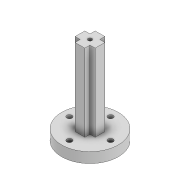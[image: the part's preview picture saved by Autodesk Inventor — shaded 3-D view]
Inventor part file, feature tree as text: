
AUTODESK INVENTOR PART (.ipt)
format: ipt  version: 2022 (Build 260153000, 153)  size: 144,896 bytes
history: native  units: mm
features: extrude x6, sketch x6, pattern_circular x1
ambient origin geometry x8: Origin, YZ Plane, XZ Plane, XY Plane, X Axis, Y Axis, Z Axis, Center Point
bodies: Solid1 (feature_tree)
feature tree (13):
  extrude  "Extrusion1"  Depth=4.0mm TaperAngle=0.0deg
  extrude  "Extrusion2"  Depth=8.0mm
  pattern_circular  "Circular Pattern1"  Count=4 Angle=360.0deg
  extrude  "Extrusion3"  Depth=7.8mm
  extrude  "Extrusion4"  Depth=2.0mm
  extrude  "Extrusion5"  Depth=3.0mm
  extrude  "Extrusion6"  Depth=8.0mm TaperAngle=0.0deg
  sketch  "Sketch1"  dims[d0=22.0mm d1=4.0mm d2=0.0mm]
  sketch  "Sketch2"  dims[d3=2.0mm d4=8.0mm]
  sketch  "Sketch3"  dims[d5=10.0mm d6=0.0mm d7=40.0mm d8=360.0deg]
  sketch  "Sketch4"  dims[d10=7.8mm d11=7.8mm]
  sketch  "Sketch5"  dims[d12=30.0mm d13=0.0mm d14=2.0mm]
  sketch  "Sketch6"  dims[d15=2.0mm d16=1.5mm d17=8.0mm d18=0.0mm d19=10.0mm d20=2.2mm d21=0.0mm d22=5.0mm d23=3.0mm d24=0.0mm]
